# Revit family: bimlib_blokirazvetviteli_vp1_sistemamrv-5-rc_haier
name_source: partatom
category: Оборудование
units: mm (PartAtom-declared; Revit-internal decimal feet)

## family parameters
Всегда вертикально = Да
На основе рабочей плоскости = Нет
Общий = Нет
При загрузке вырезать с полостями = Нет
Размер круглого соединителя = Использовать диаметр
Тип детали = Нормальный
Точка расчета площади = Нет

## types (3) — shared parameters
ADSK_Версия Revit = 2017
ADSK_Группирование = VP1 Система MRV 5-RC
ADSK_Единица измерения = шт.
ADSK_Завод-изготовитель = Haier Group
ADSK_Классификация нагрузок = ОВК
ADSK_Количество = 1
ADSK_Количество фаз = 1
ADSK_Коэффициент мощности = 1
ADSK_Наименование = Блоки-разветвители VP1 Система MRV 5-RC (с рекуперацией тепла)
ADSK_Наименование краткое = VP1 Система MRV 5-RC
ADSK_Напряжение = 230 В
ADSK_Обозначение = VP1
ADSK_Размер_Высота = 200 мм
ADSK_Размер_Глубина = 277 мм
ADSK_Размер_Ширина = 388 мм
BL_BIM library = https://bimlib.pro
HG_URL поставщика = www.haierproff.ru
URL = www.haier.com
Диаметр_Жидкость_Выход = 9.52 мм
Диаметр_Жидкость_Подача = 9.52 мм
Изготовитель = Haier Group
Частота тока = 50 Гц
zero-valued in all types: Отметка по умолчанию

## per-type parameters (varying)
| type | ADSK_Код изделия | ADSK_Масса | ADSK_Номинальная мощность | ADSK_Полная мощность | Диаметр_Газ_ВыскоеДавление_Выход | Диаметр_Газ_Выход | Диаметр_Газ_Подача | Зона обслуживания_Слева | Зона обслуживания_Справа | Потребляемая мощность |
| VP1-112B_HAIER | VP1-112B | 8.6 | 11200 Вт | 11200 В·А | 12.7 мм | 15.88 мм | 15.88 мм | 200 мм | 200 мм | 11 кВт |
| VP1-180B_HAIER | VP1-180B | 8.6 | 11200 Вт | 11200 В·А | 15.88 мм | 15.88 мм | 15.88 мм | 200 мм | 200 мм | 11 кВт |
| VP1-280B_HAIER | VP1-280B | 9.3 | 28000 Вт | 28000 В·А | 22.22 мм | 19.05 мм | 22.22 мм | 400 мм | 400 мм | 28 кВт |
